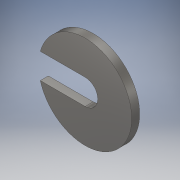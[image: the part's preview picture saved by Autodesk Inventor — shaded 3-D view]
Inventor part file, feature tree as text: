
AUTODESK INVENTOR PART (.ipt)
format: ipt  version: 2017 SP1 (Build 210196100, 196)  size: 102,912 bytes
history: native  units: in
note: dims shown in document units (in); Inventor stores cm internally (conversion verified against a paired STEP export)
features: extrude x1, sketch x1
ambient origin geometry x8: Origin, YZ Plane, XZ Plane, XY Plane, X Axis, Y Axis, Z Axis, Center Point
bodies: Solid1 (feature_tree)
feature tree (2):
  extrude  "Extrusion1"  Depth=0.3906in
  sketch  "Sketch1"  dims[d0=0.7188in d1=0.3906in d2=0.1235in d3=0.0in]
